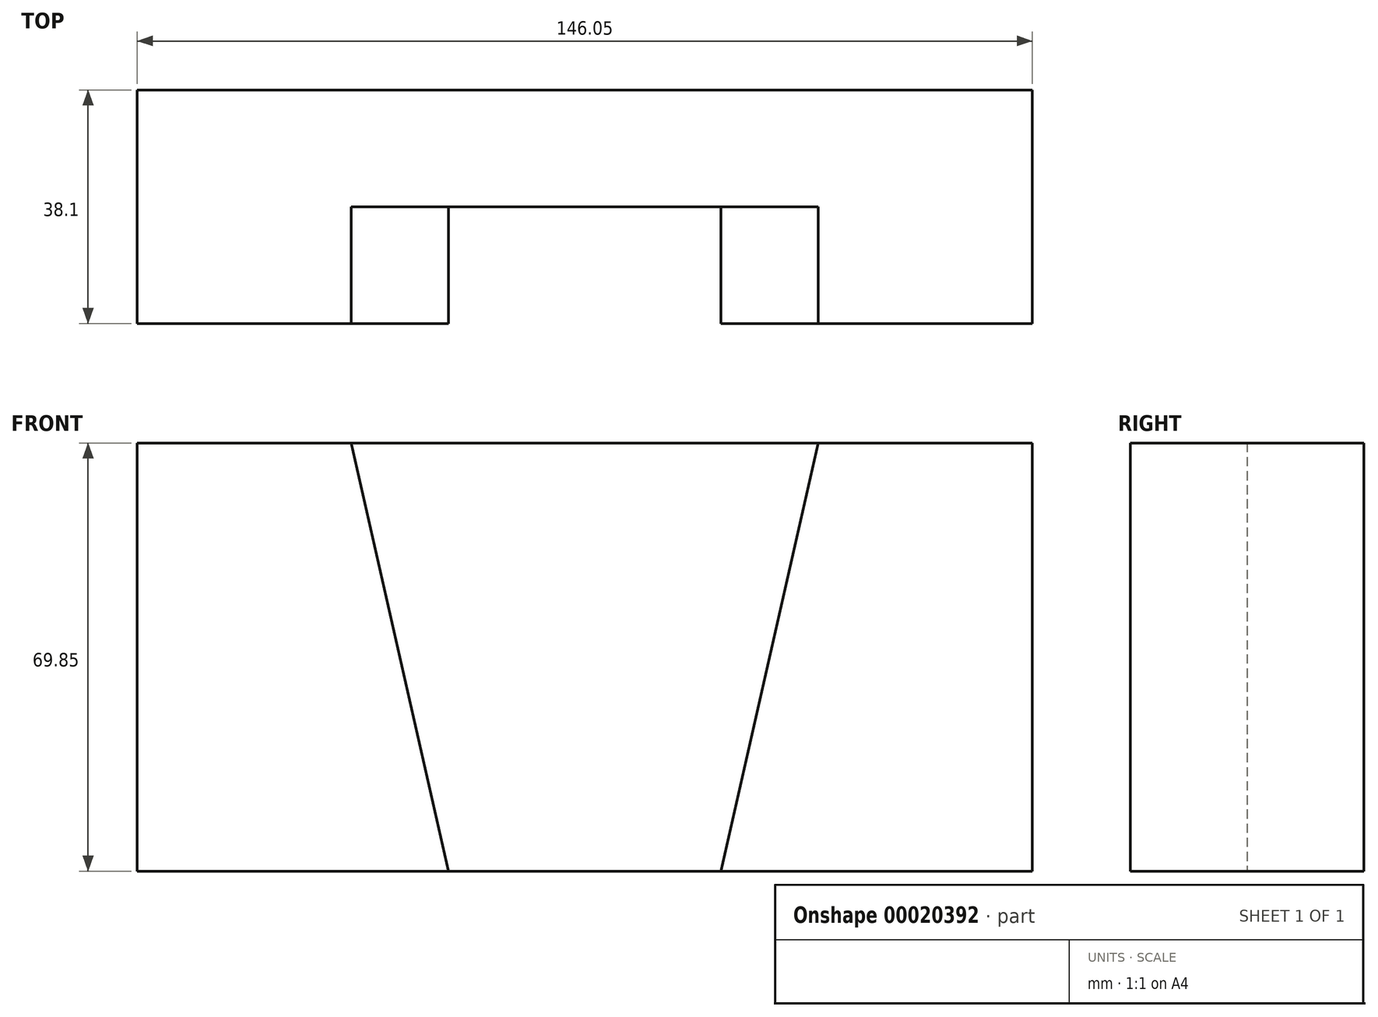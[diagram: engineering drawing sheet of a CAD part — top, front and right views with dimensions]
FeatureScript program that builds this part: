
annotation { "Feature Type Name" : "Feature", "Feature Type Description" : "" }
export const myFeature = defineFeature(function(context is Context, id is Id, definition is map)
    precondition{}
    {
        {
            var Q0;
            Q0=qCreatedBy(makeId("Front.planeOp"),FACE);
            var sketch = newSketch(context, id + "F0", { "sketchPlane" : qUnion([Q0])});
            skLineSegment(sketch, "E0.bottom", {"start": v(-68.7, 20.56) * mm, "end": v(77.35, 20.56) * mm});
            skLineSegment(sketch, "E0.top", {"start": v(-68.7, -49.29) * mm, "end": v(77.35, -49.29) * mm});
            skLineSegment(sketch, "E0.left", {"start": v(-68.7, 20.56) * mm, "end": v(-68.7, -49.29) * mm});
            skLineSegment(sketch, "E0.right", {"start": v(77.35, 20.56) * mm, "end": v(77.35, -49.29) * mm});
            skLineSegment(sketch, "E1", {"start": v(77.35, 20.56) * mm, "end": v(42.42, 20.56) * mm});
            skLineSegment(sketch, "E2", {"start": v(42.42, 20.56) * mm, "end": v(-33.78, 20.56) * mm});
            skSolve(sketch);
        }
        {
            var Q0;
            Q0=makeQuery(id+"F0.imprint","IMPRINT",FACE,{"disambiguationData":[TD([[makeQuery(id+"F0.imprint","IMPRINT",EDGE,{"derivedFrom":sQuery(id+"F0.wireOp",EDGE,"E0.bottom")}),-1.0]])]});
            extrude(context, id + "F1", {"entities" : qUnion([Q0]), "depth" : 38.1 * mm});
        }
        {
            var Q0;
            Q0=makeQuery(id+"F1.opExtrude","CAP_FACE",FACE,{"disambiguationData":[OSD([sQuery(id+"F0.wireOp",EDGE,"E0.bottom"),sQuery(id+"F0.wireOp",EDGE,"E0.top"),sQuery(id+"F0.wireOp",EDGE,"E0.left"),sQuery(id+"F0.wireOp",EDGE,"E0.right"),sQuery(id+"F0.wireOp",EDGE,"E1"),sQuery(id+"F0.wireOp",EDGE,"E2")])],"isStart":false});
            var sketch = newSketch(context, id + "F2", { "sketchPlane" : qUnion([Q0])});
            skLineSegment(sketch, "E3", {"start": v(77.35, 20.56) * mm, "end": v(42.42, 20.56) * mm});
            skLineSegment(sketch, "E4", {"start": v(77.35, -49.29) * mm, "end": v(26.55, -49.29) * mm});
            skLineSegment(sketch, "E5", {"start": v(42.42, 20.56) * mm, "end": v(26.55, -49.29) * mm});
            skLineSegment(sketch, "E6", {"start": v(-68.7, 20.56) * mm, "end": v(-33.78, 20.56) * mm});
            skLineSegment(sketch, "E7", {"start": v(-68.7, -49.29) * mm, "end": v(-17.9, -49.29) * mm});
            skLineSegment(sketch, "E8", {"start": v(-33.78, 20.56) * mm, "end": v(-17.9, -49.29) * mm});
            skSolve(sketch);
        }
        {
            var Q0;
            Q0 = qSketchRegion(id + "F2", true);
            var Q1;
            {var subQ2=sQuery(id+"F2.wireOp",EDGE,"E5");Q1=makeQuery(id+"F2.imprint","IMPRINT",FACE,{"disambiguationData":[TD([[makeQuery(id+"F2.imprint","IMPRINT",EDGE,{"derivedFrom":subQ2}),-1.0]])]});}
            extrude(context, id + "F3", {"entities" : qUnion([Q0, Q1]), "operationType" : NewBodyOperationType.REMOVE, "oppositeDirection" : true, "depth" : 19.05 * mm});
        }
    });
